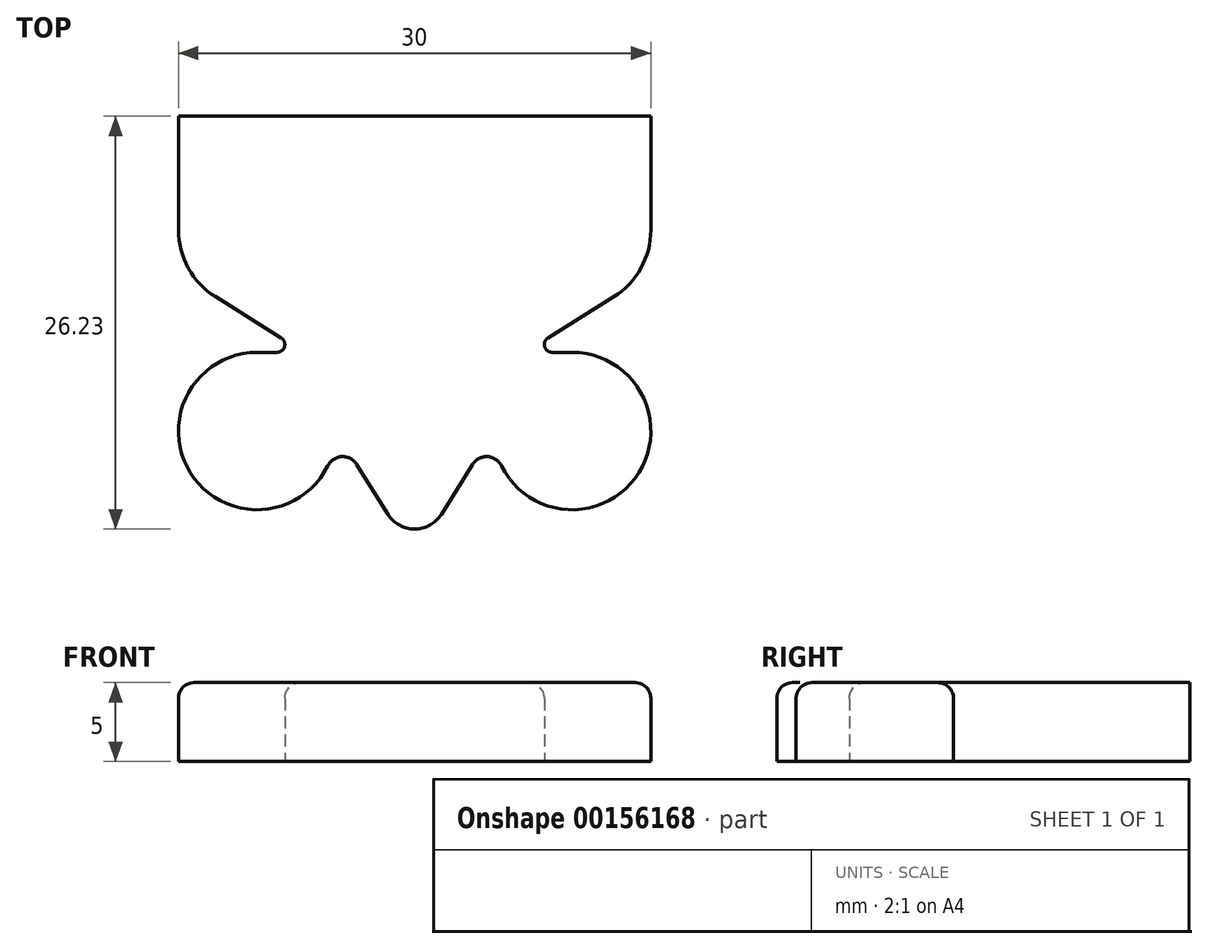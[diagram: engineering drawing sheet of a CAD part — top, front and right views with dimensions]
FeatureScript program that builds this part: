
annotation { "Feature Type Name" : "Feature", "Feature Type Description" : "" }
export const myFeature = defineFeature(function(context is Context, id is Id, definition is map)
    precondition{}
    {
        {
            var Q0;
            Q0=qCreatedBy(makeId("Top.planeOp"),FACE);
            var sketch = newSketch(context, id + "F0", { "sketchPlane" : qUnion([Q0])});
            skArc(sketch, "E0", {"start": v(-9.48, -22.21) * mm, "mid": v(-0.75, -22.64) * mm, "end": v(-5, -15) * mm});
            skLineSegment(sketch, "E1", {"start": v(0, 0) * mm, "end": v(0, -7.23) * mm});
            skLineSegment(sketch, "E2", {"start": v(-30, 0) * mm, "end": v(-30, -7.23) * mm});
            skArc(sketch, "E3", {"start": v(-25, -15) * mm, "mid": v(-29.25, -22.64) * mm, "end": v(-20.52, -22.21) * mm});
            skLineSegment(sketch, "E4", {"start": v(-30, 0) * mm, "end": v(0, 0) * mm});
            skLineSegment(sketch, "E5", {"start": v(-27.65, -11.47) * mm, "end": v(-23.48, -14.08) * mm});
            skLineSegment(sketch, "E6", {"start": v(-2.35, -11.47) * mm, "end": v(-6.52, -14.08) * mm});
            skLineSegment(sketch, "E7", {"start": v(-23.74, -15) * mm, "end": v(-25, -15) * mm});
            skLineSegment(sketch, "E8", {"start": v(-6.26, -15) * mm, "end": v(-5, -15) * mm});
            skLineSegment(sketch, "E9", {"start": v(-18.68, -22.12) * mm, "end": v(-16.7, -25.29) * mm});
            skLineSegment(sketch, "E10", {"start": v(-13.3, -25.29) * mm, "end": v(-11.32, -22.12) * mm});
            skPoint(sketch, "E11.visualSharp", {"position": v(-30, -10) * mm});
            skArc(sketch, "E11.filletArc", {"start": v(-30, -7.23) * mm, "mid": v(-29.37, -9.65) * mm, "end": v(-27.65, -11.47) * mm});
            skPoint(sketch, "E12.visualSharp", {"position": v(0, -10) * mm});
            skArc(sketch, "E12.filletArc", {"start": v(-2.35, -11.47) * mm, "mid": v(-0.63, -9.65) * mm, "end": v(0, -7.23) * mm});
            skPoint(sketch, "E13.visualSharp", {"position": v(-15, -28) * mm});
            skArc(sketch, "E13.filletArc", {"start": v(-16.7, -25.29) * mm, "mid": v(-15, -26.23) * mm, "end": v(-13.3, -25.29) * mm});
            skPoint(sketch, "E14.visualSharp", {"position": v(-20, -20) * mm});
            skArc(sketch, "E14.filletArc", {"start": v(-18.68, -22.12) * mm, "mid": v(-19.62, -21.63) * mm, "end": v(-20.52, -22.21) * mm});
            skPoint(sketch, "E15.visualSharp", {"position": v(-10, -20) * mm});
            skArc(sketch, "E15.filletArc", {"start": v(-9.48, -22.21) * mm, "mid": v(-10.38, -21.63) * mm, "end": v(-11.32, -22.12) * mm});
            skPoint(sketch, "E16.visualSharp", {"position": v(-22, -15) * mm});
            skArc(sketch, "E16.filletArc", {"start": v(-23.74, -15) * mm, "mid": v(-23.26, -14.64) * mm, "end": v(-23.48, -14.08) * mm});
            skPoint(sketch, "E17.visualSharp", {"position": v(-8, -15) * mm});
            skArc(sketch, "E17.filletArc", {"start": v(-6.52, -14.08) * mm, "mid": v(-6.74, -14.64) * mm, "end": v(-6.26, -15) * mm});
            skSolve(sketch);
        }
        {
            var Q0;
            Q0=makeQuery(id+"F0.imprint","IMPRINT",FACE,{"disambiguationData":[TD([[makeQuery(id+"F0.imprint","IMPRINT",EDGE,{"derivedFrom":sQuery(id+"F0.wireOp",EDGE,"E0")}),1.0]])]});
            extrude(context, id + "F1", {"entities" : qUnion([Q0]), "depth" : 5 * mm});
        }
        {
            var Q0;
            Q0=makeQuery(id+"F1.opExtrude","CAP_EDGE",EDGE,{"disambiguationData":[OSD([sQuery(id+"F0.wireOp",EDGE,"E3")])],"isStart":false});
            fillet(context, id + "F2", {"entities" : qUnion([Q0]), "radius" : 1 * mm, "tangentPropagation" : true, "allowEdgeOverflow" : false});
        }
    });
